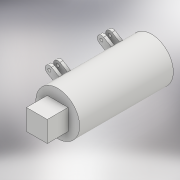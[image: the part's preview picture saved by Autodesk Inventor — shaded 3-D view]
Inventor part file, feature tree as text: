
AUTODESK INVENTOR PART (.ipt)
format: ipt  version: 2018 (Build 220112000, 112)  size: 173,568 bytes
history: native  units: mm
features: extrude x3, sketch x2, pattern_linear x2, plane x1
ambient origin geometry x8: Origin, YZ Plane, XZ Plane, XY Plane, X Axis, Y Axis, Z Axis, Center Point
bodies: Solid1 (feature_tree)
feature tree (8):
  sketch  "Sketch1"  dims[d0=42.0mm d1=20.0mm]
  extrude  "Extrusion1"  Depth=20.0mm
  extrude  "Extrusion2"  Depth=90.0mm TaperAngle=0.0deg
  plane  "Work Plane1"
  extrude  "Extrusion3"  Depth=20.0mm TaperAngle=0.0deg
  pattern_linear  "Rectangular Pattern2"  Spacing1=-20.0mm  [1 undecoded]
  pattern_linear  "Rectangular Pattern1"  Spacing1=3.0mm  [1 undecoded]
  sketch  "Sketch2"  dims[d2=20.0mm d3=90.0mm d4=0.0mm d5=20.0mm d6=0.0mm d7=-20.0mm d8=3.0mm d9=30.0mm d10=15.0mm d11=4.0mm d12=4.0mm d13=4.0mm d14=3.0mm d15=0.0mm d16=20.0mm d18=50.0mm d19=20.0mm d21=8.0mm]
note: 2 required parameter values undecoded (feature->parameter linkage not recoverable at this tier; creation-order binding heuristic only, values carry confidence <= 0.55)
